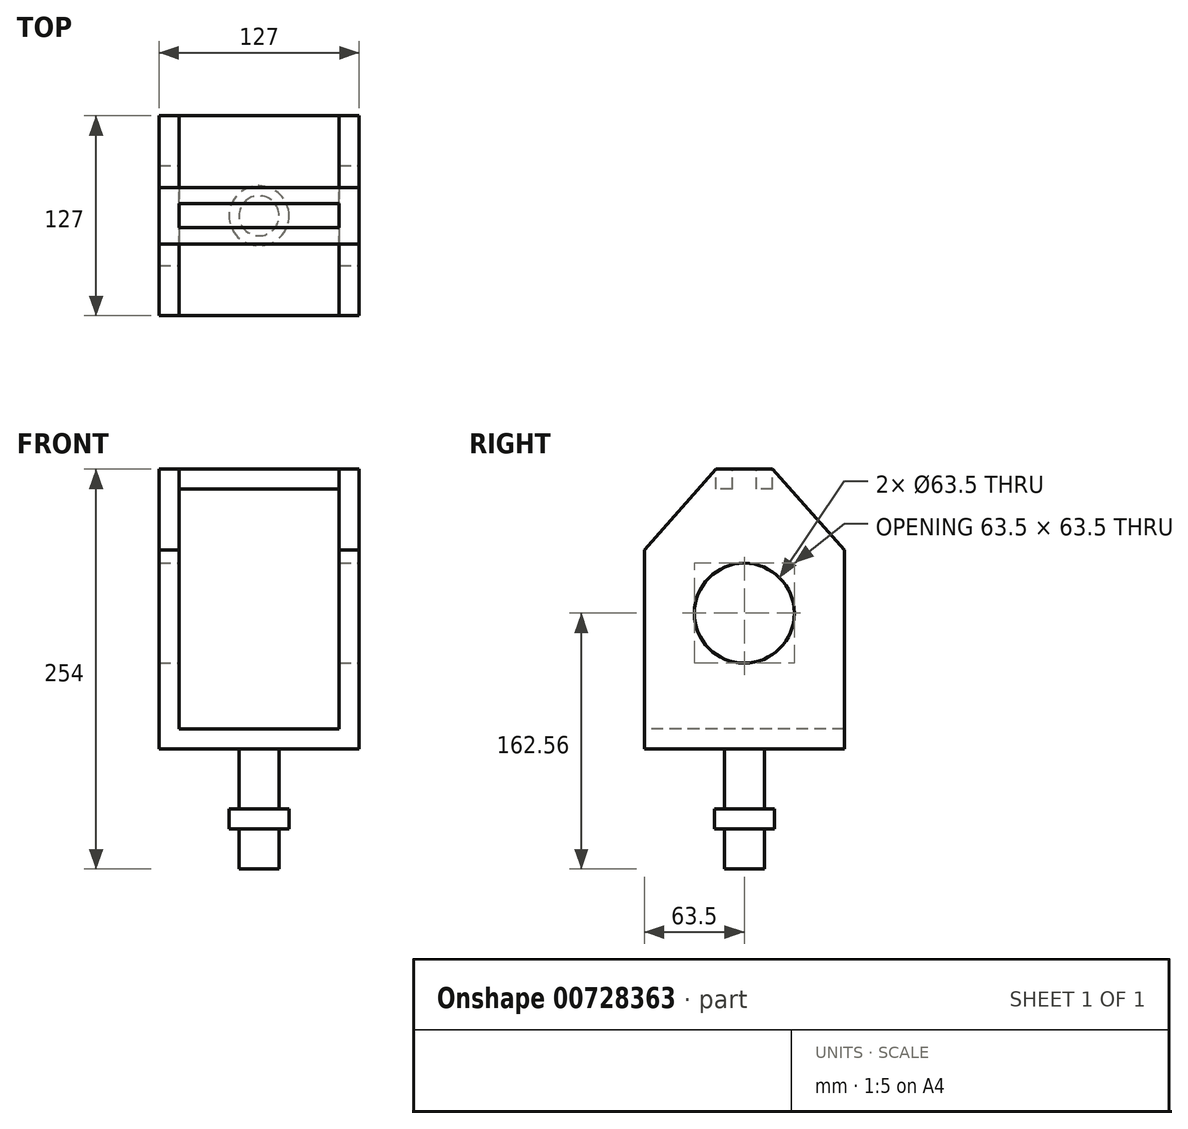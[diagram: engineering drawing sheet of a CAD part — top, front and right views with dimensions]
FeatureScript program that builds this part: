
annotation { "Feature Type Name" : "Feature", "Feature Type Description" : "" }
export const myFeature = defineFeature(function(context is Context, id is Id, definition is map)
    precondition{}
    {
        {
            var Q0;
            Q0=qCreatedBy(makeId("Top.planeOp"),FACE);
            var sketch = newSketch(context, id + "F0", { "sketchPlane" : qUnion([Q0])});
            skLineSegment(sketch, "E0.bottom", {"start": v(63.5, 63.5) * mm, "end": v(-63.5, 63.5) * mm});
            skLineSegment(sketch, "E0.top", {"start": v(63.5, -63.5) * mm, "end": v(-63.5, -63.5) * mm});
            skLineSegment(sketch, "E0.left", {"start": v(63.5, 63.5) * mm, "end": v(63.5, -63.5) * mm});
            skLineSegment(sketch, "E0.right", {"start": v(-63.5, 63.5) * mm, "end": v(-63.5, -63.5) * mm});
            skPoint(sketch, "E0.middle", {"position": v(0, 0) * mm});
            skSolve(sketch);
        }
        {
            var Q0;
            Q0 = qSketchRegion(id + "F0", true);
            extrude(context, id + "F1", {"entities" : qUnion([Q0]), "depth" : 254 * mm, "offsetDistance" : 25.4 * mm});
        }
        {
            var Q0;
            Q0=qCreatedBy(makeId("Front.planeOp"),FACE);
            var sketch = newSketch(context, id + "F2", { "sketchPlane" : qUnion([Q0])});
            skLineSegment(sketch, "E1", {"start": v(12.7, 0) * mm, "end": v(12.7, 25.4) * mm});
            skLineSegment(sketch, "E2", {"start": v(12.7, 25.4) * mm, "end": v(19.05, 25.4) * mm});
            skLineSegment(sketch, "E3", {"start": v(19.05, 25.4) * mm, "end": v(19.05, 38.1) * mm});
            skLineSegment(sketch, "E4", {"start": v(19.05, 38.1) * mm, "end": v(12.7, 38.1) * mm});
            skLineSegment(sketch, "E5", {"start": v(12.7, 38.1) * mm, "end": v(12.7, 76.2) * mm});
            skLineSegment(sketch, "E6", {"start": v(12.7, 76.2) * mm, "end": v(118.23, 76.2) * mm});
            skLineSegment(sketch, "E7", {"start": v(118.23, 76.2) * mm, "end": v(118.23, 0) * mm});
            skLineSegment(sketch, "E8", {"start": v(118.23, 0) * mm, "end": v(12.7, 0) * mm});
            skLineSegment(sketch, "E9", {"start": v(0, 0) * mm, "end": v(0, 254.66) * mm});
            skSolve(sketch);
        }
        {
            var Q0;
            Q0 = qSketchRegion(id + "F2", true);
            var Q1;
            Q1=sQuery(id+"F2.wireOp",EDGE,"E9");
            revolve(context, id + "F3", {"operationType" : NewBodyOperationType.REMOVE, "surfaceOperationType" : NewSurfaceOperationType.NEW, "entities" : qUnion([Q0]), "axis" : qUnion([Q1]), "revolveType" : RevolveType.FULL, "oppositeDirection" : true});
        }
        {
            var Q0;
            Q0=makeQuery(id+"F1.opExtrude","SWEPT_FACE",FACE,{"disambiguationData":[OSD([sQuery(id+"F0.wireOp",EDGE,"E0.top")])]});
            cPlane(context, id + "F4", {"entities" : qUnion([Q0]), "cplaneType" : CPlaneType.OFFSET, "offset" : 0 * mm, "width" : 152.4 * mm, "height" : 152.4 * mm});
        }
        {
            var Q0;
            Q0=qCreatedBy(id+"F4.planeOp",FACE);
            var sketch = newSketch(context, id + "F5", { "sketchPlane" : qUnion([Q0])});
            skLineSegment(sketch, "E10.bottom", {"start": v(-50.8, 241.3) * mm, "end": v(50.8, 241.3) * mm});
            skLineSegment(sketch, "E10.top", {"start": v(-50.8, 88.9) * mm, "end": v(50.8, 88.9) * mm});
            skLineSegment(sketch, "E10.left", {"start": v(-50.8, 241.3) * mm, "end": v(-50.8, 88.9) * mm});
            skLineSegment(sketch, "E10.right", {"start": v(50.8, 241.3) * mm, "end": v(50.8, 88.9) * mm});
            skSolve(sketch);
        }
        {
            var Q0;
            Q0 = qSketchRegion(id + "F5", true);
            var Q1;
            Q1=makeQuery(id+"F1.opExtrude","SWEPT_FACE",FACE,{"disambiguationData":[OSD([sQuery(id+"F0.wireOp",EDGE,"E0.bottom")])]});
            extrude(context, id + "F6", {"entities" : qUnion([Q0]), "operationType" : NewBodyOperationType.REMOVE, "endBound" : BoundingType.UP_TO_SURFACE, "oppositeDirection" : true, "depth" : 25.4 * mm, "endBoundEntityFace" : qUnion([Q1]), "offsetDistance" : 25.4 * mm});
        }
        {
            var Q0;
            Q0=makeQuery(id+"F1.opExtrude","SWEPT_FACE",FACE,{"disambiguationData":[OSD([sQuery(id+"F0.wireOp",EDGE,"E0.left")])]});
            cPlane(context, id + "F7", {"entities" : qUnion([Q0]), "cplaneType" : CPlaneType.OFFSET, "offset" : 0 * mm, "width" : 152.4 * mm, "height" : 152.4 * mm});
        }
        {
            var Q0;
            Q0=qCreatedBy(id+"F7.planeOp",FACE);
            var sketch = newSketch(context, id + "F8", { "sketchPlane" : qUnion([Q0])});
            skLineSegment(sketch, "E11", {"start": v(-66.5, 199.42) * mm, "end": v(-11.48, 261.36) * mm});
            skLineSegment(sketch, "E12", {"start": v(-67.36, 261.36) * mm, "end": v(-66.5, 199.42) * mm});
            skLineSegment(sketch, "E13", {"start": v(-67.36, 261.36) * mm, "end": v(-11.48, 261.36) * mm});
            skLineSegment(sketch, "E14.MirrorCS", {"start": v(66.5, 199.42) * mm, "end": v(11.48, 261.36) * mm});
            skLineSegment(sketch, "E15.MirrorCS", {"start": v(67.36, 261.36) * mm, "end": v(11.48, 261.36) * mm});
            skLineSegment(sketch, "E16.MirrorCS", {"start": v(67.36, 261.36) * mm, "end": v(66.5, 199.42) * mm});
            skCircle(sketch, "E17", {"center": v(0, 162.56) * mm, "radius": 31.75 * mm});
            skSolve(sketch);
        }
        {
            var Q0;
            Q0=makeQuery(id+"F8.imprint","IMPRINT",FACE,{"disambiguationData":[TD([[makeQuery(id+"F8.imprint","IMPRINT",EDGE,{"derivedFrom":sQuery(id+"F8.wireOp",EDGE,"E11")}),1.0]])]});
            var Q1;
            Q1=makeQuery(id+"F8.imprint","IMPRINT",FACE,{"disambiguationData":[TD([[makeQuery(id+"F8.imprint","IMPRINT",EDGE,{"derivedFrom":sQuery(id+"F8.wireOp",EDGE,"E14.MirrorCS")}),-1.0]])]});
            var Q2;
            Q2=makeQuery(id+"F8.imprint","IMPRINT",FACE,{"disambiguationData":[TD([[makeQuery(id+"F8.imprint","IMPRINT",EDGE,{"derivedFrom":sQuery(id+"F8.wireOp",EDGE,"E17")}),1.0]])]});
            extrude(context, id + "F9", {"entities" : qUnion([Q0, Q1, Q2]), "operationType" : NewBodyOperationType.REMOVE, "oppositeDirection" : true, "depth" : 254 * mm, "offsetDistance" : 25.4 * mm});
        }
        {
            var Q0;
            Q0=makeQuery(id+"F1.opExtrude","CAP_FACE",FACE,{"disambiguationData":[OSD([sQuery(id+"F0.wireOp",EDGE,"E0.bottom"),sQuery(id+"F0.wireOp",EDGE,"E0.top"),sQuery(id+"F0.wireOp",EDGE,"E0.left"),sQuery(id+"F0.wireOp",EDGE,"E0.right")])],"isStart":false});
            cPlane(context, id + "F10", {"entities" : qUnion([Q0]), "cplaneType" : CPlaneType.OFFSET, "offset" : 0 * mm, "width" : 152.4 * mm, "height" : 152.4 * mm});
        }
        {
            var Q0;
            Q0=qCreatedBy(id+"F10.planeOp",FACE);
            var sketch = newSketch(context, id + "F11", { "sketchPlane" : qUnion([Q0])});
            skLineSegment(sketch, "E18.bottom", {"start": v(-50.8, 18.02) * mm, "end": v(50.8, 18.02) * mm});
            skLineSegment(sketch, "E18.top", {"start": v(-50.8, 43.94) * mm, "end": v(50.8, 43.94) * mm});
            skLineSegment(sketch, "E18.left", {"start": v(-50.8, 18.02) * mm, "end": v(-50.8, 43.94) * mm});
            skLineSegment(sketch, "E18.right", {"start": v(50.8, 18.02) * mm, "end": v(50.8, 43.94) * mm});
            skLineSegment(sketch, "E19.MirrorCS", {"start": v(-50.8, -43.94) * mm, "end": v(50.8, -43.94) * mm});
            skLineSegment(sketch, "E20.MirrorCS", {"start": v(-50.8, -18.02) * mm, "end": v(50.8, -18.02) * mm});
            skLineSegment(sketch, "E21.MirrorCS", {"start": v(-50.8, -18.02) * mm, "end": v(-50.8, -43.94) * mm});
            skLineSegment(sketch, "E22.MirrorCS", {"start": v(50.8, -18.02) * mm, "end": v(50.8, -43.94) * mm});
            skPoint(sketch, "E23.firstSnap0", {"position": v(-50.8, 30.98) * mm});
            skLineSegment(sketch, "E23.bottom", {"start": v(-50.8, 7.62) * mm, "end": v(50.8, 7.62) * mm});
            skLineSegment(sketch, "E23.top", {"start": v(-50.8, 0) * mm, "end": v(50.8, 0) * mm});
            skLineSegment(sketch, "E23.left", {"start": v(-50.8, 7.62) * mm, "end": v(-50.8, 0) * mm});
            skLineSegment(sketch, "E23.right", {"start": v(50.8, 7.62) * mm, "end": v(50.8, 0) * mm});
            skLineSegment(sketch, "E24.MirrorCS", {"start": v(-50.8, -7.62) * mm, "end": v(50.8, -7.62) * mm});
            skLineSegment(sketch, "E25.MirrorCS", {"start": v(-50.8, -7.62) * mm, "end": v(-50.8, 0) * mm});
            skLineSegment(sketch, "E26.MirrorCS", {"start": v(50.8, -7.62) * mm, "end": v(50.8, 0) * mm});
            skSolve(sketch);
        }
        {
            var Q0;
            Q0 = qSketchRegion(id + "F11", true);
            extrude(context, id + "F12", {"entities" : qUnion([Q0]), "operationType" : NewBodyOperationType.REMOVE, "oppositeDirection" : true, "depth" : 25.4 * mm, "offsetDistance" : 25.4 * mm});
        }
    });
